# Revit family: 54-3132-001 DN1200
name_source: partatom
category: Pipe Accessories
units: mm (PartAtom-declared; Revit-internal decimal feet)

## family parameters
Always vertical = No
Cut with Voids When Loaded = No
Part Type = Valve - Breaks Into
Round Connector Dimension = Use Diameter
Shared = No
Work Plane-Based = No

## types (9) — shared parameters
1 = 1 mm  [stored 0.00328084 ft]
10 = 10 mm  [stored 0.0328084 ft]
54-1200-31-0302100 = DN1200_ PN10_ CTC
54-1200-31-0303100 = DN1200_ PN10_ CTC
54-1200-31-0304100 = DN1200_ PN10_ CTC
54-1200-31-1302100 = DN1200_ PN16_ CTC
54-1200-31-1303100 = DN1200_ PN16_ CTC
54-1200-31-1304100 = DN1200_ PN16_ CTC
54-1200-32-0302100 = DN1200_ PN10_ CTO
54-1200-32-1302100 = DN1200_ PN16_ CTO
54-1200-32-1304100 = DN1200_ PN16_ CTO
ADN = 1200 mm
BP_centre = 14.5 mm  [stored 0.0475722 ft]
Body_H = 1213.5 mm
Body_L = 1352 mm
Body_T = 592.5 mm
Body_W = 418.5 mm
Bonnet_FL_L = 1690 mm
Bonnet_FL_W = 558 mm
Bonnet_dim1 = 270.4 mm
Bonnet_dim2 = 146.48 mm
Bonnet_dim3 = 2087.22 mm
Bonnet_fillet = 46.5 mm  [stored 0.152559 ft]
Bypass_L = 106 mm  [stored 0.347769 ft]
Bypass_Location = 259 mm
Bypass_R = 29 mm  [stored 0.0951444 ft]
Bypass_R1 = 58 mm  [stored 0.190289 ft]
Bypass_W = 90 mm  [stored 0.295276 ft]
Description_ = AVK METAL SEAT GATE VALVE, FLANGED, PN 10/16
Fillet = 139.5 mm
H = 782 mm
H1 = 2427 mm
H2 = 773 mm
L = 914 mm
OD = 1546 mm
OD1 = 1546 mm
Raised_dia = 1328 mm
Raised_dis = 5 mm  [stored 0.0164042 ft]
Rib_Actual = 856 mm
Rib_H = 970.8 mm
Rib_H1 = 300 mm
Rib_H2 = 780 mm
Rib_H3 = 930 mm
Rib_H4 = 1080 mm
Rib_L = 760.5 mm
Rib_W = 251.1 mm
Search_table = 54-3132-001 DN1200
URL product pages = https://www.avkvalves.com
W = 1712 mm
W1 = 694 mm
W_half = 1018 mm
bottom_rib = 773 mm
sweep = 6 mm  [stored 0.019685 ft]
wedge_dim1 = 460.35 mm
zero-valued in all types: Default Elevation

## per-type parameters (varying)
| type | ACtuator_T | Actuator_FLR | Actuator_dim1 | Actuator_dim2 | Body_rib_T | Bonnet_FL_T | Bore | Cut_dis | DN | F | F1 | F2 | FL_T | PN | Stem_dim | stem_dim | stem_dim1 |
| 54-1200-31-0302100 | 32.4 mm  [stored 0.106299 ft] | 105 mm  [stored 0.344488 ft] | 63 mm  [stored 0.206693 ft] | 37.8 mm  [stored 0.124016 ft] | 18 mm  [stored 0.0590551 ft] | 85.5 mm  [stored 0.280512 ft] | 600 mm | 42.75 mm  [stored 0.140256 ft] | 1200 mm | 42 mm  [stored 0.137795 ft] | 18.9 mm  [stored 0.0620079 ft] | 136 mm | 45 mm  [stored 0.147638 ft] | 10 mm  [stored 0.0328084 ft] | 52.5 mm  [stored 0.172244 ft] | 45.33 mm | 68.25 mm  [stored 0.223917 ft] |
| 54-1200-31-0303100 | 32.4 mm  [stored 0.106299 ft] | 150 mm | 90 mm  [stored 0.295276 ft] | 54 mm  [stored 0.177165 ft] | 18 mm  [stored 0.0590551 ft] | 85.5 mm  [stored 0.280512 ft] | 600.05 mm | 42.75 mm  [stored 0.140256 ft] | 1200.1 mm | 60 mm  [stored 0.19685 ft] | 27 mm  [stored 0.0885827 ft] | 176 mm | 45 mm  [stored 0.147638 ft] | 10 mm  [stored 0.0328084 ft] | 75 mm | 58.67 mm | 97.5 mm  [stored 0.319882 ft] |
| 54-1200-31-0304100 | 32.4 mm  [stored 0.106299 ft] | 175 mm | 105 mm  [stored 0.344488 ft] | 63 mm  [stored 0.206693 ft] | 18 mm  [stored 0.0590551 ft] | 85.5 mm  [stored 0.280512 ft] | 600.06 mm | 42.75 mm  [stored 0.140256 ft] | 1200.11 mm | 70 mm  [stored 0.229659 ft] | 31.5 mm  [stored 0.103346 ft] | 206 mm | 45 mm  [stored 0.147638 ft] | 10 mm  [stored 0.0328084 ft] | 87.5 mm  [stored 0.287073 ft] | 68.67 mm | 113.75 mm |
| 54-1200-31-1302100 | 41.04 mm  [stored 0.134646 ft] | 105 mm  [stored 0.344488 ft] | 63 mm  [stored 0.206693 ft] | 37.8 mm  [stored 0.124016 ft] | 22.8 mm  [stored 0.0748031 ft] | 108.3 mm  [stored 0.355315 ft] | 600.06 mm | 54.15 mm  [stored 0.177657 ft] | 1200.12 mm | 42 mm  [stored 0.137795 ft] | 18.9 mm  [stored 0.0620079 ft] | 136 mm | 57 mm  [stored 0.187008 ft] | 16 mm  [stored 0.0524934 ft] | 52.5 mm  [stored 0.172244 ft] | 45.33 mm | 68.25 mm  [stored 0.223917 ft] |
| 54-1200-31-1303100 | 41.04 mm  [stored 0.134646 ft] | 150 mm | 90 mm  [stored 0.295276 ft] | 54 mm  [stored 0.177165 ft] | 22.8 mm  [stored 0.0748031 ft] | 108.3 mm  [stored 0.355315 ft] | 600.07 mm | 54.15 mm  [stored 0.177657 ft] | 1200.13 mm | 60 mm  [stored 0.19685 ft] | 27 mm  [stored 0.0885827 ft] | 176 mm | 57 mm  [stored 0.187008 ft] | 16 mm  [stored 0.0524934 ft] | 75 mm | 58.67 mm | 97.5 mm  [stored 0.319882 ft] |
| 54-1200-31-1304100 | 41.04 mm  [stored 0.134646 ft] | 175 mm | 105 mm  [stored 0.344488 ft] | 63 mm  [stored 0.206693 ft] | 22.8 mm  [stored 0.0748031 ft] | 108.3 mm  [stored 0.355315 ft] | 600.07 mm | 54.15 mm  [stored 0.177657 ft] | 1200.14 mm | 70 mm  [stored 0.229659 ft] | 31.5 mm  [stored 0.103346 ft] | 206 mm | 57 mm  [stored 0.187008 ft] | 16 mm  [stored 0.0524934 ft] | 87.5 mm  [stored 0.287073 ft] | 68.67 mm | 113.75 mm |
| 54-1200-32-0302100 | 32.4 mm  [stored 0.106299 ft] | 105 mm  [stored 0.344488 ft] | 63 mm  [stored 0.206693 ft] | 37.8 mm  [stored 0.124016 ft] | 18 mm  [stored 0.0590551 ft] | 85.5 mm  [stored 0.280512 ft] | 600.08 mm | 42.75 mm  [stored 0.140256 ft] | 1200.15 mm | 42 mm  [stored 0.137795 ft] | 18.9 mm  [stored 0.0620079 ft] | 136 mm | 45 mm  [stored 0.147638 ft] | 10 mm  [stored 0.0328084 ft] | 52.5 mm  [stored 0.172244 ft] | 45.33 mm | 68.25 mm  [stored 0.223917 ft] |
| 54-1200-32-1302100 | 41.04 mm  [stored 0.134646 ft] | 105 mm  [stored 0.344488 ft] | 63 mm  [stored 0.206693 ft] | 37.8 mm  [stored 0.124016 ft] | 22.8 mm  [stored 0.0748031 ft] | 108.3 mm  [stored 0.355315 ft] | 600.08 mm | 54.15 mm  [stored 0.177657 ft] | 1200.16 mm | 42 mm  [stored 0.137795 ft] | 18.9 mm  [stored 0.0620079 ft] | 136 mm | 57 mm  [stored 0.187008 ft] | 16 mm  [stored 0.0524934 ft] | 52.5 mm  [stored 0.172244 ft] | 45.33 mm | 68.25 mm  [stored 0.223917 ft] |
| 54-1200-32-1304100 | 41.04 mm  [stored 0.134646 ft] | 175 mm | 105 mm  [stored 0.344488 ft] | 63 mm  [stored 0.206693 ft] | 22.8 mm  [stored 0.0748031 ft] | 108.3 mm  [stored 0.355315 ft] | 600.09 mm | 54.15 mm  [stored 0.177657 ft] | 1200.17 mm | 70 mm  [stored 0.229659 ft] | 31.5 mm  [stored 0.103346 ft] | 206 mm | 57 mm  [stored 0.187008 ft] | 16 mm  [stored 0.0524934 ft] | 87.5 mm  [stored 0.287073 ft] | 68.67 mm | 113.75 mm |

note: [stored X ft] marks values corroborated as IEEE doubles in the binary element streams (Revit-internal decimal feet)

## geometry (parser evidence)
native form markers: Sweep x4
no freeform markers — native parametric forms only
